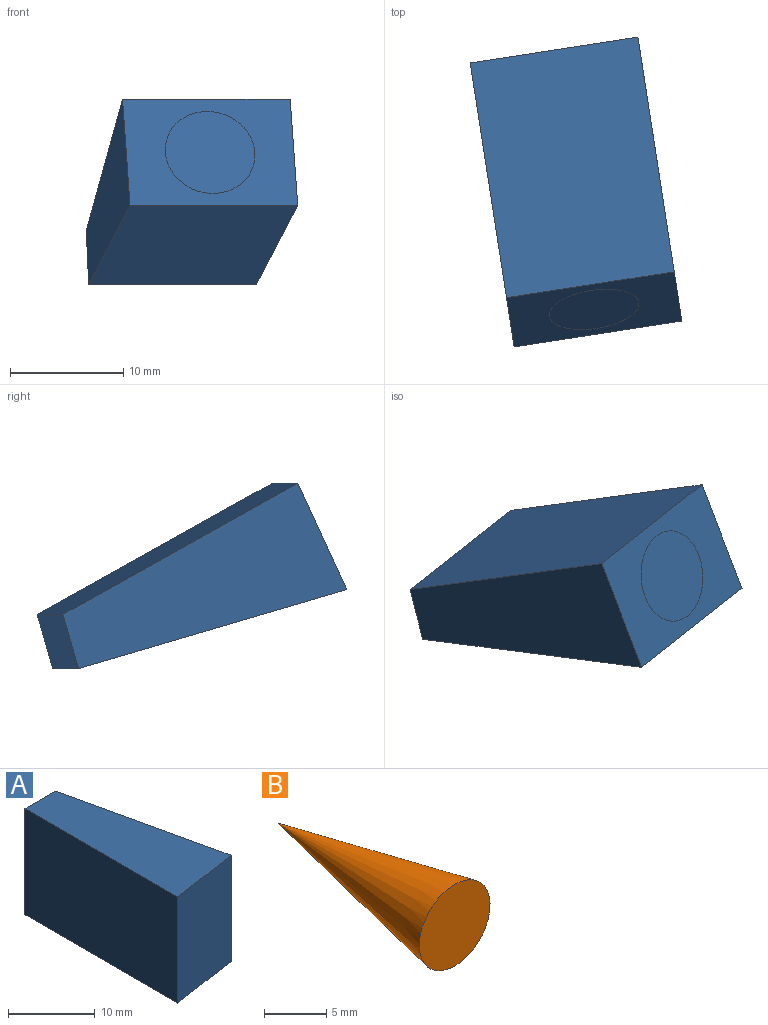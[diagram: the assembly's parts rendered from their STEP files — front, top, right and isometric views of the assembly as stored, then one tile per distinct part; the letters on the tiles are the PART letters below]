
ASSEMBLY  parts=2 mates=1
PART A: 6 faces, bbox 10.2x25x15 mm
  f0: plane 15x10.25mm, normal (0.15,-0.99,0), area 155.5mm2, adj f1,f3,f4,f5
  f1: plane 23.42x15mm, normal (0.98,0.22,0), area 360mm2, adj f0,f2,f4,f5
  f2: plane 15x5mm, normal (0,1,0), area 75mm2, adj f1,f3,f4,f5
  f3: plane 25x15mm, normal (-1,0,0), area 375mm2, adj f0,f2,f4,f5
  f4: plane 25x10.25mm, normal (0,0,1), area 186.6mm2, adj f0,f1,f2,f3
  f5: plane 25x10.25mm, normal (0,0,-1), area 186.6mm2, adj f0,f1,f2,f3
PART B: 2 faces, bbox 8x20x8 mm
  f0: cone r=0mm half-angle=11.3deg, axis (0,-1,0), area 256.3mm2, adj f1
  f1: plane 8x8mm, normal (0,-1,0), area 50.3mm2, adj f0
PLACE A rot(axis=(-0.06,-0.98,0.21),92.7deg) t=(-25.57,-2.97,55.6)mm
PLACE B rot(axis=(-0.94,-0.07,0.33),26.5deg) t=(-1.11,32.98,-5.45)mm
MATE fastened A.f0 <-> B.f0  axis (0.14,-0.9,0.42) through (-35.36,11.34,2.09)mm
